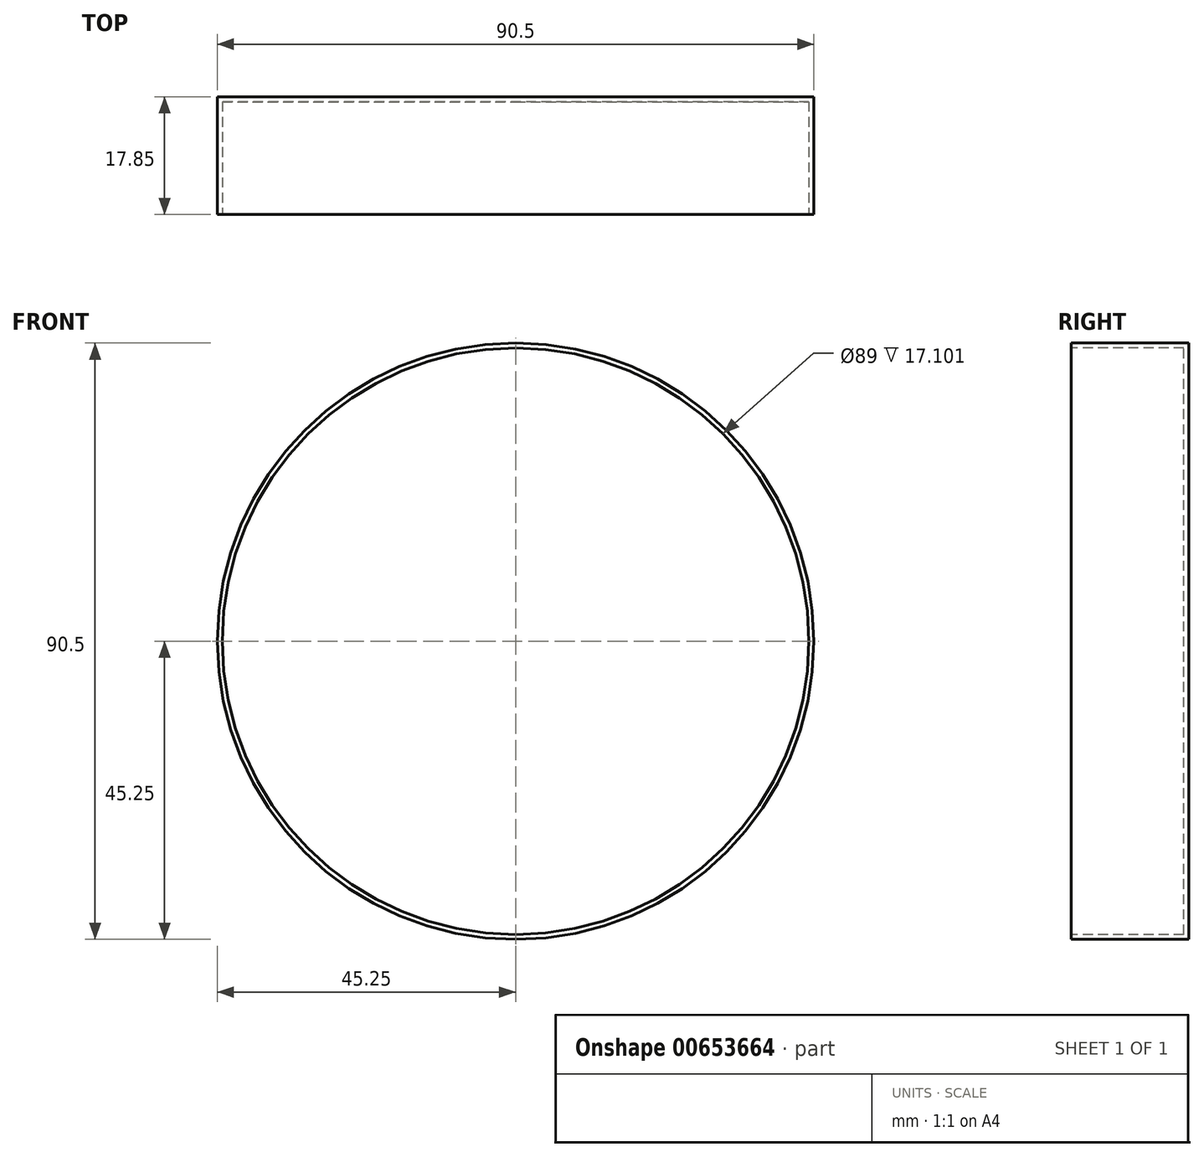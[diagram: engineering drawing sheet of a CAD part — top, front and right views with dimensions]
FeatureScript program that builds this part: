
annotation { "Feature Type Name" : "Feature", "Feature Type Description" : "" }
export const myFeature = defineFeature(function(context is Context, id is Id, definition is map)
    precondition{}
    {
        {
            var Q0;
            Q0=qCreatedBy(makeId("Top.planeOp"),FACE);
            var sketch = newSketch(context, id + "F0", { "sketchPlane" : qUnion([Q0])});
            skLineSegment(sketch, "E0", {"start": v(-70, 0) * mm, "end": v(70, 0) * mm});
            skLineSegment(sketch, "E1", {"start": v(-45.25, 17.85) * mm, "end": v(-45.25, 0) * mm});
            skLineSegment(sketch, "E2", {"start": v(-45.25, 0) * mm, "end": v(-44.5, 0) * mm});
            skLineSegment(sketch, "E3", {"start": v(-45.25, 17.85) * mm, "end": v(0, 17.85) * mm});
            skLineSegment(sketch, "E4", {"start": v(0, 17.85) * mm, "end": v(0, 17.1) * mm});
            skLineSegment(sketch, "E5", {"start": v(-44.5, 17.1) * mm, "end": v(0, 17.1) * mm});
            skLineSegment(sketch, "E6", {"start": v(-44.5, 17.1) * mm, "end": v(-44.5, 0) * mm});
            skLineSegment(sketch, "E7", {"start": v(0, -70) * mm, "end": v(0, 70) * mm});
            skSolve(sketch);
        }
        {
            var Q0;
            Q0=makeQuery(id+"F0.imprint","IMPRINT",FACE,{"disambiguationData":[TD([[makeQuery(id+"F0.imprint","IMPRINT",EDGE,{"derivedFrom":sQuery(id+"F0.wireOp",EDGE,"E1")}),1.0]])]});
            var Q1;
            Q1=sQuery(id+"F0.wireOp",EDGE,"E7");
            revolve(context, id + "F1", {"entities" : qUnion([Q0]), "axis" : qUnion([Q1]), "revolveType" : RevolveType.FULL});
        }
    });
